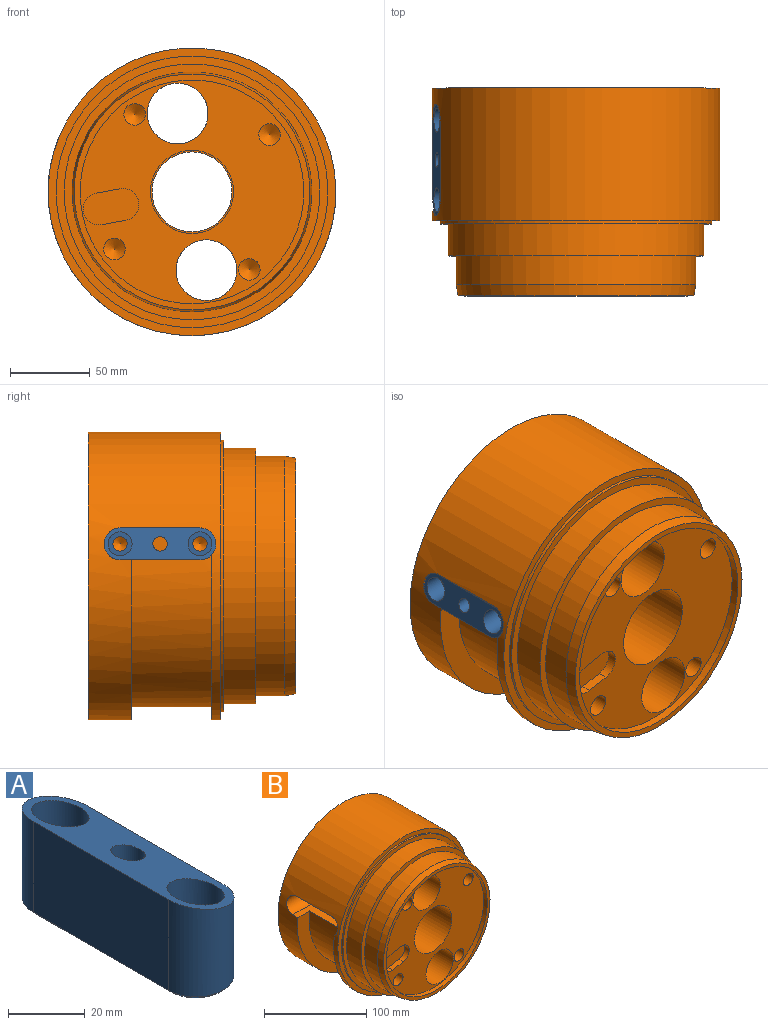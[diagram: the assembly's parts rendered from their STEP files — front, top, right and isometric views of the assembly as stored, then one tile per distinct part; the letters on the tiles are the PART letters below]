
ASSEMBLY  parts=2 mates=1
PART A: 17 faces, bbox 20.8x70.8x30.8 mm
  f0: cylinder r=4.5mm len=16mm, axis (0,0,1), area 452.4mm2, adj f6,f11
  f1: cylinder r=4.5mm len=16mm, axis (0,0,1), area 452.4mm2, adj f6,f9
  f2: cylinder r=10mm len=29mm, axis (0,0,-1), area 832.5mm2, adj f3,f5,f12,f14
  f3: plane 50x24mm, normal (1,0,0), area 1200mm2, adj f2,f4,f12,f13
  f4: cylinder r=10mm len=29mm, axis (0,0,-1), area 832.5mm2, adj f3,f5,f12,f15
  f5: plane 50x29mm, normal (-1,0,0), area 1450mm2, adj f2,f4,f12,f16
  f6: plane 68x18mm, normal (0,0,-1), area 963.6mm2, adj f0,f1,f7,f13,f14,f15,f16
  f7: cylinder r=4.5mm len=28.63mm, axis (0,0,-1), area 777.5mm2, adj f6,f12
  f8: cylinder r=7.5mm len=15mm, axis (0,0,1), area 541.9mm2, adj f9,f12
  f9: plane 15x15mm, normal (0,0,1), area 113.1mm2, adj f1,f8
  f10: cylinder r=7.5mm len=15mm, axis (0,0,1), area 541.9mm2, adj f11,f12
  f11: plane 15x15mm, normal (0,0,1), area 113.1mm2, adj f0,f10
  f12: plane 70.79x20.79mm, normal (0.24,0,0.97), area 924.7mm2, adj f2,f3,f4,f5,f7,f8,f10
  f13: plane 50x1mm, normal (0.71,0,-0.71), area 70.7mm2, adj f3,f6,f14,f15
  f14: cone r=10mm half-angle=45deg, axis (0,0,1), area 42.2mm2, adj f2,f6,f13,f16
  f15: cone r=10mm half-angle=45deg, axis (0,0,1), area 42.2mm2, adj f4,f6,f13,f16
  f16: plane 50x1mm, normal (-0.71,0,-0.71), area 70.7mm2, adj f5,f6,f14,f15
PART B: 59 faces, bbox 180x130x180 mm
  f0: plane 155x155mm, normal (0,1,0), area 13450.8mm2, adj f15,f16,f19,f20,f30,f32,f34,f36
  f1: plane 140x140mm, normal (0,-1,0), area 9815.1mm2, adj f12,f13,f19,f20,f38,f40,f42,f44
  f2: cylinder r=90mm len=180mm, axis (0,1,0), area 30939.7mm2, adj f3,f4,f21,f22,f23,f24,f26,f27
  f3: plane 180x180mm, normal (0,-1,0), area 2748.9mm2, adj f2,f5
  f4: plane 180x180mm, normal (0,1,0), area 2802.3mm2, adj f2,f17
  f5: cylinder r=85mm len=170mm, axis (0,1,0), area 1068.1mm2, adj f3,f6
  f6: plane 170x170mm, normal (0,-1,0), area 2591.8mm2, adj f5,f7
  f7: cylinder r=80mm len=160mm, axis (0,1,0), area 10053.1mm2, adj f6,f8
  f8: plane 160x160mm, normal (0,-1,0), area 2434.7mm2, adj f7,f9
  f9: cylinder r=75mm len=150mm, axis (0,1,0), area 8482.3mm2, adj f8,f11
  f10: plane 147.53x147.53mm, normal (0,-1,0), area 1700.8mm2, adj f11,f12
  f11: cone r=73.77mm half-angle=10deg, axis (0,1,0), area 3322mm2, adj f9,f10
  f12: cylinder r=70mm len=140mm, axis (0,-1,0), area 2199.1mm2, adj f1,f10
  f13: cylinder r=26mm len=115mm, axis (0,-1,0), area 18786.7mm2, adj f1,f14
  f14: plane 52x52mm, normal (0,-1,0), area 160.2mm2, adj f13,f15
  f15: cylinder r=25mm len=50mm, axis (0,1,0), area 1570.8mm2, adj f0,f14
  f16: cylinder r=77.5mm len=155mm, axis (0,1,0), area 2264.3mm2, adj f0,f18
  f17: cylinder r=84.9mm len=169.8mm, axis (0,1,0), area 2480.5mm2, adj f4,f18
  f18: plane 169.8x169.8mm, normal (0,1,0), area 3775.4mm2, adj f16,f17
  f19: cylinder r=19mm len=125mm, axis (0,1,0), area 14922.6mm2, adj f0,f1
  f20: cylinder r=19mm len=125mm, axis (0,1,0), area 14922.6mm2, adj f0,f1
  f21: plane 50x25.35mm, normal (0,0,-1), area 1267.6mm2, adj f2,f22,f24,f25
  f22: cylinder r=10mm len=29.58mm, axis (-1,0,0), area 753.5mm2, adj f2,f21,f23,f25,f26,f28
  f23: plane 50x29.94mm, normal (0,0,1), area 806.8mm2, adj f2,f22,f24,f25,f27,f28
  f24: cylinder r=10mm len=29.94mm, axis (-1,0,0), area 878mm2, adj f2,f21,f23,f25
  f25: plane 70x20mm, normal (-1,0,0), area 1186.9mm2, adj f21,f22,f23,f24,f56,f58
  f26: plane 180x102.86mm, normal (0,1,0), area 2367.5mm2, adj f2,f22,f28
  f27: plane 180x100mm, normal (0,-1,0), area 2321.6mm2, adj f2,f23,f28
  f28: cylinder r=82mm len=164mm, axis (0,1,0), area 13388.1mm2, adj f2,f22,f23,f26,f27
  f29: cone r=0mm half-angle=59deg, axis (0,1,0), area 167mm2, adj f30
  f30: cylinder r=6.75mm len=30mm, axis (0,1,0), area 1272.3mm2, adj f0,f29
  f31: cone r=0mm half-angle=59deg, axis (0,1,0), area 167mm2, adj f32
  f32: cylinder r=6.75mm len=30mm, axis (0,1,0), area 1272.3mm2, adj f0,f31
  f33: cone r=0mm half-angle=59deg, axis (0,1,0), area 167mm2, adj f34
  f34: cylinder r=6.75mm len=30mm, axis (0,1,0), area 1272.3mm2, adj f0,f33
  f35: cone r=0mm half-angle=59deg, axis (0,1,0), area 167mm2, adj f36
  f36: cylinder r=6.75mm len=30mm, axis (0,1,0), area 1272.3mm2, adj f0,f35
  f37: cone r=0mm half-angle=59deg, axis (0,-1,0), area 167mm2, adj f38
  f38: cylinder r=6.75mm len=35mm, axis (0,-1,0), area 1484.4mm2, adj f1,f37
  f39: cone r=0mm half-angle=59deg, axis (0,-1,0), area 167mm2, adj f40
  f40: cylinder r=6.75mm len=35mm, axis (0,-1,0), area 1484.4mm2, adj f1,f39
  f41: cone r=0mm half-angle=59deg, axis (0,-1,0), area 167mm2, adj f42
  f42: cylinder r=6.75mm len=35mm, axis (0,-1,0), area 1484.4mm2, adj f1,f41
  f43: cone r=0mm half-angle=59deg, axis (0,-1,0), area 167mm2, adj f44
  f44: cylinder r=6.75mm len=35mm, axis (0,-1,0), area 1484.4mm2, adj f1,f43
  f45: plane 14.75x6mm, normal (0.18,0,-0.98), area 90mm2, adj f1,f46,f48,f49
  f46: cylinder r=10mm len=19.84mm, axis (0,-1,0), area 188.5mm2, adj f1,f45,f47,f49
  f47: plane 14.75x6mm, normal (-0.18,0,0.98), area 90mm2, adj f1,f46,f48,f49
  f48: cylinder r=10mm len=19.84mm, axis (0,-1,0), area 188.5mm2, adj f1,f45,f47,f49
  f49: plane 34.75x22.71mm, normal (0,-1,0), area 614.2mm2, adj f45,f46,f47,f48
  f50: plane 14.75x6mm, normal (0.18,0,-0.98), area 90mm2, adj f0,f51,f53,f54
  f51: cylinder r=10mm len=19.84mm, axis (0,1,0), area 188.5mm2, adj f0,f50,f52,f54
  f52: plane 14.75x6mm, normal (-0.18,0,0.98), area 90mm2, adj f0,f51,f53,f54
  f53: cylinder r=10mm len=19.84mm, axis (0,1,0), area 188.5mm2, adj f0,f50,f52,f54
  f54: plane 34.75x22.71mm, normal (0,1,0), area 614.2mm2, adj f50,f51,f52,f53
  f55: cone r=0mm half-angle=59deg, axis (-1,0,0), area 74.2mm2, adj f56
  f56: cylinder r=4.5mm len=20mm, axis (-1,0,0), area 565.5mm2, adj f25,f55
  f57: cone r=0mm half-angle=59deg, axis (-1,0,0), area 74.2mm2, adj f58
  f58: cylinder r=4.5mm len=20mm, axis (-1,0,0), area 565.5mm2, adj f25,f57
PLACE A rot(axis=(0,-1,0),90deg) t=(-139.02,-44.07,-7.24)mm
PLACE B t=(-79.52,0.93,-27.24)mm fixed
MATE fastened B.f22 <-> A.f0  axis (-1,0,0) through (-139.02,-69.07,-7.24)mm
